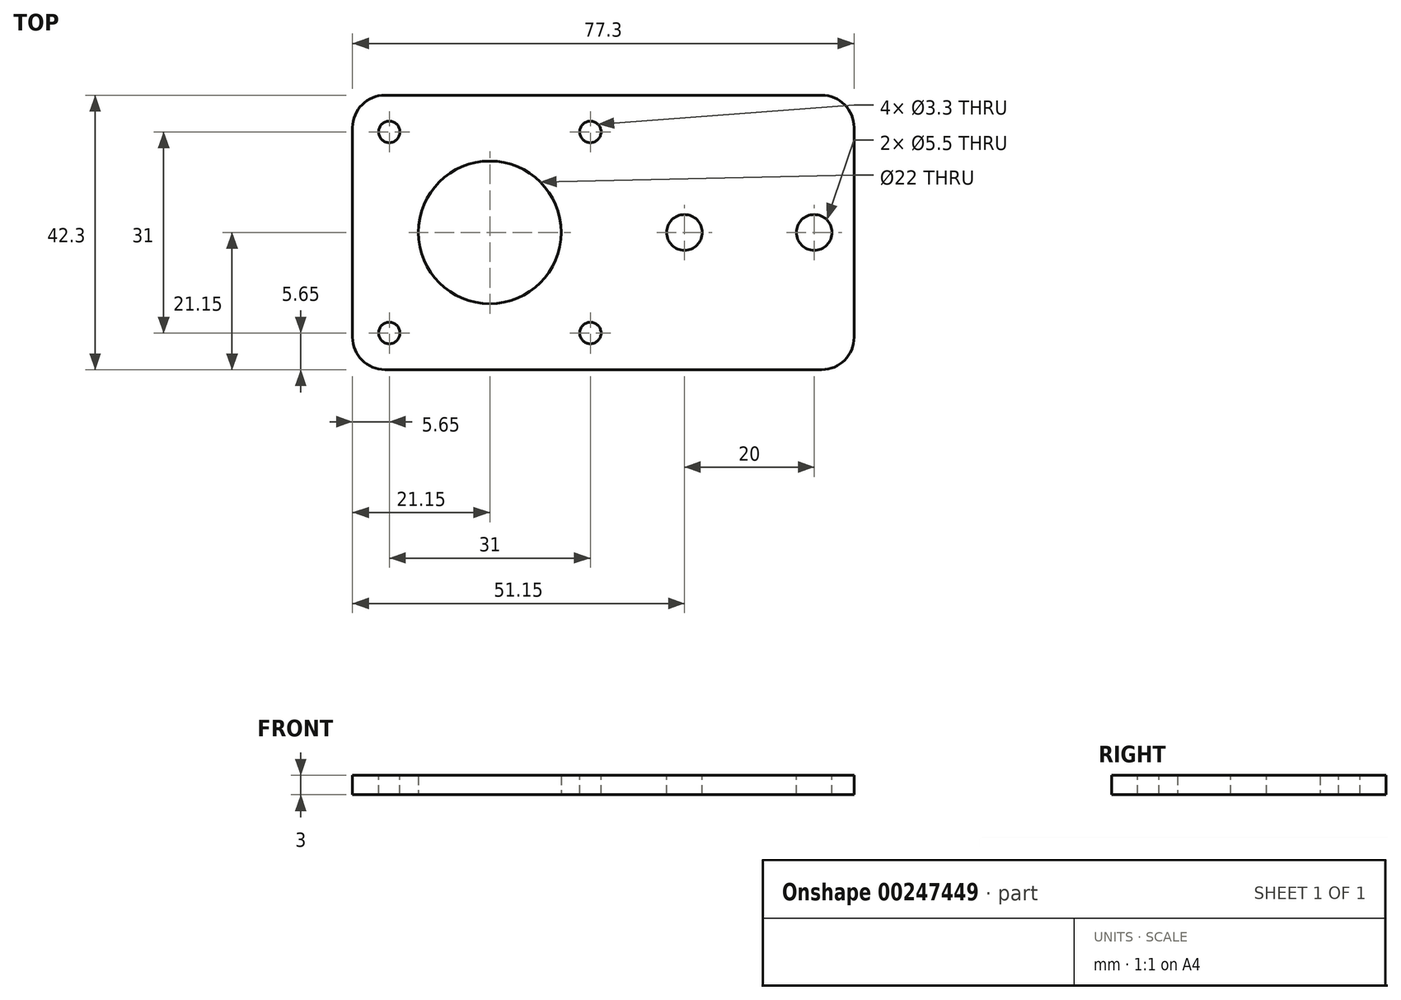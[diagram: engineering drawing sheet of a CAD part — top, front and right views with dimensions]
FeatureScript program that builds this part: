
annotation { "Feature Type Name" : "Feature", "Feature Type Description" : "" }
export const myFeature = defineFeature(function(context is Context, id is Id, definition is map)
    precondition{}
    {
        {
            var Q0;
            Q0=qCreatedBy(makeId("Top.planeOp"),FACE);
            var sketch = newSketch(context, id + "F0", { "sketchPlane" : qUnion([Q0])});
            skLineSegment(sketch, "E0.bottom", {"start": v(0, 0) * mm, "end": v(77.3, 0) * mm});
            skLineSegment(sketch, "E0.top", {"start": v(0, 42.3) * mm, "end": v(77.3, 42.3) * mm});
            skLineSegment(sketch, "E0.left", {"start": v(0, 0) * mm, "end": v(0, 42.3) * mm});
            skLineSegment(sketch, "E0.right", {"start": v(77.3, 0) * mm, "end": v(77.3, 42.3) * mm});
            skCircle(sketch, "E1", {"center": v(21.15, 21.15) * mm, "radius": 11 * mm});
            skPoint(sketch, "E2", {"position": v(5.65, 5.65) * mm});
            skPoint(sketch, "E3", {"position": v(36.65, 5.65) * mm});
            skLineSegment(sketch, "E4", {"start": v(0, 21.15) * mm, "end": v(21.15, 21.15) * mm});
            skPoint(sketch, "E5.MirrorP", {"position": v(36.65, 36.65) * mm});
            skPoint(sketch, "E6.MirrorP", {"position": v(5.65, 36.65) * mm});
            skSolve(sketch);
        }
        {
            var Q0;
            {var subQ3=sQuery(id+"F0.wireOp",EDGE,"E0.bottom");Q0=makeQuery(id+"F0.imprint","IMPRINT",FACE,{"disambiguationData":[TD([[makeQuery(id+"F0.imprint","IMPRINT",EDGE,{"derivedFrom":subQ3}),1.0]])]});}
            extrude(context, id + "F1", {"entities" : qUnion([Q0]), "depth" : 3 * mm});
        }
        {
            var Q0;
            Q0=makeQuery(id+"F1.opExtrude","CAP_FACE",FACE,{"disambiguationData":[OSD([sQuery(id+"F0.wireOp",EDGE,"E0.bottom"),sQuery(id+"F0.wireOp",EDGE,"E0.top"),sQuery(id+"F0.wireOp",EDGE,"E0.left"),sQuery(id+"F0.wireOp",EDGE,"E0.right"),sQuery(id+"F0.wireOp",EDGE,"E1")])],"isStart":false});
            var sketch = newSketch(context, id + "F2", { "sketchPlane" : qUnion([Q0])});
            skPoint(sketch, "E7", {"position": v(5.65, 5.65) * mm});
            skPoint(sketch, "E8", {"position": v(21.15, 21.15) * mm});
            skLineSegment(sketch, "E9", {"start": v(21.15, 21.15) * mm, "end": v(0, 21.15) * mm});
            skLineSegment(sketch, "E10", {"start": v(21.15, 21.15) * mm, "end": v(21.15, 0) * mm});
            skPoint(sketch, "E11.MirrorP", {"position": v(5.65, 36.65) * mm});
            skPoint(sketch, "E12.MirrorP", {"position": v(36.65, 36.65) * mm});
            skPoint(sketch, "E13.MirrorP", {"position": v(36.65, 5.65) * mm});
            skSolve(sketch);
        }
        {
            var Q0;
            Q0=sQuery(id+"F2.wireOp",VERTEX,"E11.MirrorP");
            var Q1;
            Q1=sQuery(id+"F2.wireOp",VERTEX,"E12.MirrorP");
            var Q2;
            Q2=sQuery(id+"F2.wireOp",VERTEX,"E13.MirrorP");
            var Q3;
            Q3=sQuery(id+"F2.wireOp",VERTEX,"E7");
            var Q4;
            Q4=makeQuery(id+"F1.opExtrude","SWEPT_BODY",BODY,{"disambiguationData":[OSD([sQuery(id+"F0.wireOp",EDGE,"E0.bottom"),sQuery(id+"F0.wireOp",EDGE,"E0.top"),sQuery(id+"F0.wireOp",EDGE,"E0.left"),sQuery(id+"F0.wireOp",EDGE,"E0.right"),sQuery(id+"F0.wireOp",EDGE,"E1")])]});
            hole(context, id + "F3", {"style" : HoleStyle.SIMPLE, "endStyle" : HoleEndStyle.THROUGH, "standardTappedOrClearance" : lookupTablePath({ "standard" : "ISO", "fit" : "Normal", "size" : "M3", "type" : "Clearance" }), "standardBlindInLast" : lookupTablePath({ "fit" : "Standard", "standard" : "ISO", "size" : "M3", "type" : "Clearance" }), "holeDiameter" : 3.3 * mm, "tappedDepth" : 12 * mm, "tapClearance" : 3, "locations" : qUnion([Q0, Q1, Q2, Q3]), "scope" : qUnion([Q4])});
        }
        {
            var Q0;
            Q0=makeQuery(id+"F1.opExtrude","CAP_FACE",FACE,{"disambiguationData":[OSD([sQuery(id+"F0.wireOp",EDGE,"E0.bottom"),sQuery(id+"F0.wireOp",EDGE,"E0.top"),sQuery(id+"F0.wireOp",EDGE,"E0.left"),sQuery(id+"F0.wireOp",EDGE,"E0.right"),sQuery(id+"F0.wireOp",EDGE,"E1")])],"isStart":false});
            var sketch = newSketch(context, id + "F4", { "sketchPlane" : qUnion([Q0])});
            skPoint(sketch, "E14", {"position": v(51.15, 21.15) * mm});
            skPoint(sketch, "E15", {"position": v(71.15, 21.15) * mm});
            skPoint(sketch, "E16", {"position": v(21.15, 21.15) * mm});
            skSolve(sketch);
        }
        {
            var Q0;
            Q0=sQuery(id+"F4.wireOp",VERTEX,"E14");
            var Q1;
            Q1=sQuery(id+"F4.wireOp",VERTEX,"E15");
            var Q2;
            Q2=makeQuery(id+"F1.opExtrude","SWEPT_BODY",BODY,{"disambiguationData":[OSD([sQuery(id+"F0.wireOp",EDGE,"E0.bottom"),sQuery(id+"F0.wireOp",EDGE,"E0.top"),sQuery(id+"F0.wireOp",EDGE,"E0.left"),sQuery(id+"F0.wireOp",EDGE,"E0.right"),sQuery(id+"F0.wireOp",EDGE,"E1")])]});
            hole(context, id + "F5", {"style" : HoleStyle.SIMPLE, "endStyle" : HoleEndStyle.THROUGH, "standardTappedOrClearance" : lookupTablePath({ "standard" : "ISO", "fit" : "Normal", "size" : "M5", "type" : "Clearance" }), "standardBlindInLast" : lookupTablePath({ "fit" : "Standard", "standard" : "ISO", "size" : "M5", "type" : "Clearance" }), "holeDiameter" : 5.5 * mm, "tappedDepth" : 12 * mm, "tapClearance" : 3, "locations" : qUnion([Q0, Q1]), "scope" : qUnion([Q2])});
        }
        {
            var Q0;
            Q0=makeQuery(id+"F1.opExtrude","SWEPT_EDGE",EDGE,{"disambiguationData":[OSD([sQuery(id+"F0.wireOp",EDGE,"E0.bottom"),sQuery(id+"F0.wireOp",EDGE,"E0.right")])]});
            var Q1;
            Q1=makeQuery(id+"F1.opExtrude","SWEPT_EDGE",EDGE,{"disambiguationData":[OSD([sQuery(id+"F0.wireOp",EDGE,"E0.bottom"),sQuery(id+"F0.wireOp",EDGE,"E0.left")])]});
            var Q2;
            Q2=makeQuery(id+"F1.opExtrude","SWEPT_EDGE",EDGE,{"disambiguationData":[OSD([sQuery(id+"F0.wireOp",EDGE,"E0.top"),sQuery(id+"F0.wireOp",EDGE,"E0.right")])]});
            var Q3;
            Q3=makeQuery(id+"F1.opExtrude","SWEPT_EDGE",EDGE,{"disambiguationData":[OSD([sQuery(id+"F0.wireOp",EDGE,"E0.top"),sQuery(id+"F0.wireOp",EDGE,"E0.left")])]});
            fillet(context, id + "F6", {"entities" : qUnion([Q0, Q1, Q2, Q3]), "radius" : 5 * mm, "tangentPropagation" : true, "allowEdgeOverflow" : false});
        }
    });
